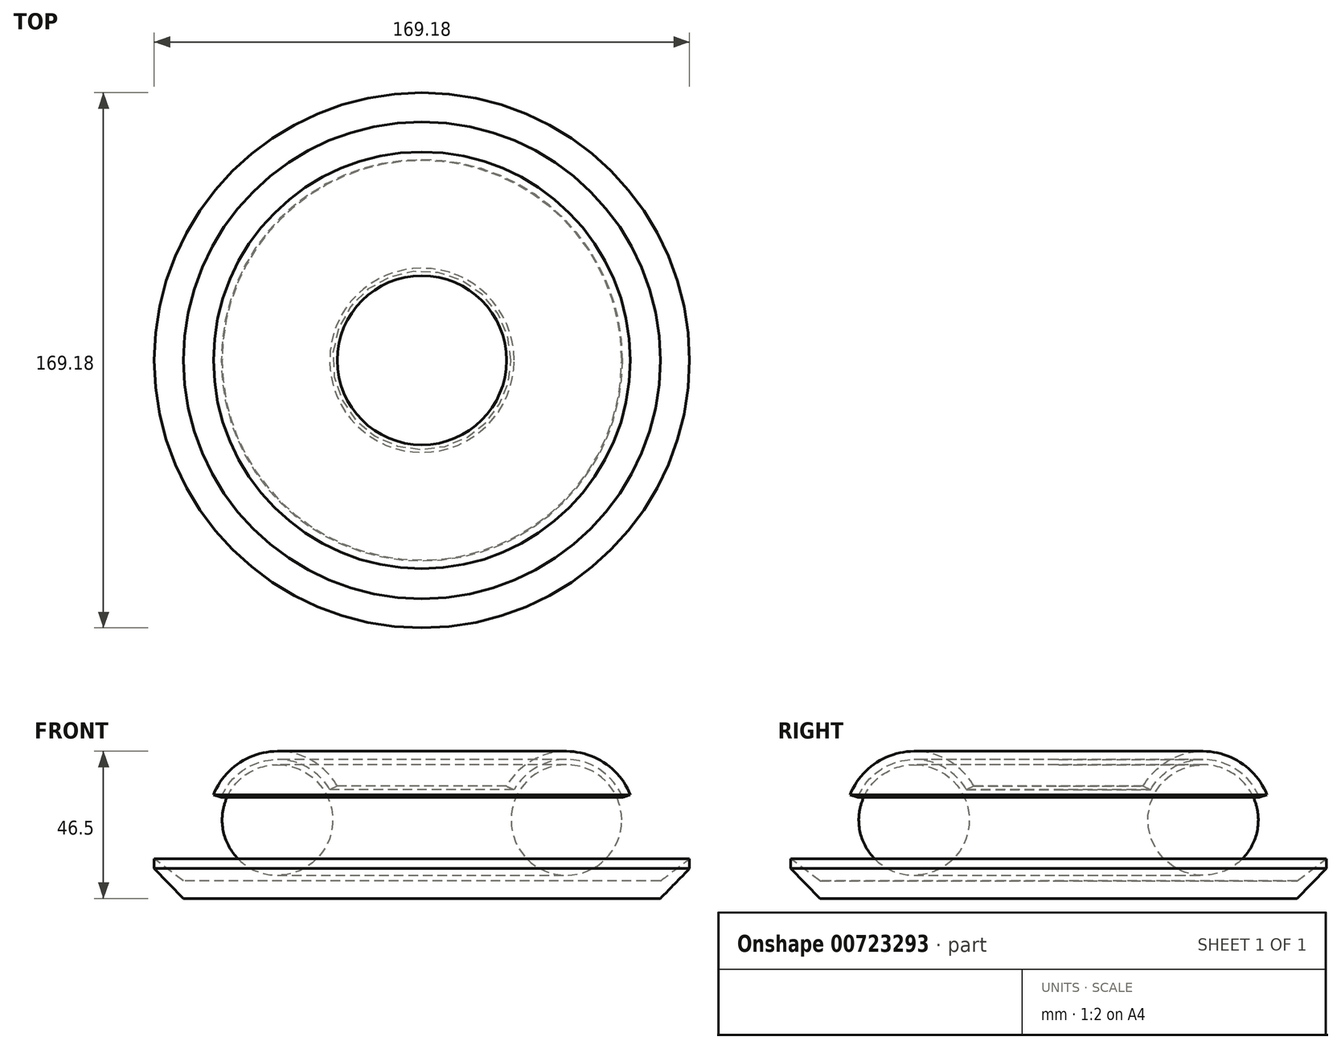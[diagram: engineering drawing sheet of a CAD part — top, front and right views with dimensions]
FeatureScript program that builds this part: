
annotation { "Feature Type Name" : "Feature", "Feature Type Description" : "" }
export const myFeature = defineFeature(function(context is Context, id is Id, definition is map)
    precondition{}
    {
        {
            var Q0;
            Q0=qCreatedBy(makeId("Right.planeOp"),FACE);
            var sketch = newSketch(context, id + "F0", { "sketchPlane" : qUnion([Q0])});
            skCircle(sketch, "E0", {"center": v(45.66, 0) * mm, "radius": 17.47 * mm});
            skLineSegment(sketch, "E1", {"start": v(0, 46.44) * mm, "end": v(0, -54.2) * mm, "construction": true});
            skArc(sketch, "E2", {"start": v(65.86, 7.98) * mm, "mid": v(47.15, 21.67) * mm, "end": v(26.74, 10.67) * mm});
            skArc(sketch, "E3", {"start": v(29.12, 9.6) * mm, "mid": v(47.03, 19.08) * mm, "end": v(63.4, 7.14) * mm});
            skLineSegment(sketch, "E4", {"start": v(26.74, 10.67) * mm, "end": v(29.12, 9.6) * mm});
            skLineSegment(sketch, "E5", {"start": v(65.86, 7.98) * mm, "end": v(63.4, 7.14) * mm});
            skLineSegment(sketch, "E6", {"start": v(0, -19.25) * mm, "end": v(75.37, -19.25) * mm});
            skLineSegment(sketch, "E7", {"start": v(75.37, -19.25) * mm, "end": v(84.59, -12.29) * mm});
            skLineSegment(sketch, "E8", {"start": v(84.59, -12.29) * mm, "end": v(84.59, -15.36) * mm});
            skLineSegment(sketch, "E9", {"start": v(84.59, -15.36) * mm, "end": v(75.37, -24.78) * mm});
            skLineSegment(sketch, "E10", {"start": v(75.37, -24.78) * mm, "end": v(0, -24.78) * mm});
            skLineSegment(sketch, "E11", {"start": v(0, -19.25) * mm, "end": v(0, -24.78) * mm});
            skSolve(sketch);
        }
        {
            var Q0;
            Q0=makeQuery(id+"F0.imprint","IMPRINT",FACE,{"disambiguationData":[TD([[makeQuery(id+"F0.imprint","IMPRINT",EDGE,{"derivedFrom":sQuery(id+"F0.wireOp",EDGE,"E2")}),1.0]])]});
            var Q1;
            Q1=makeQuery(id+"F0.imprint","IMPRINT",FACE,{"disambiguationData":[TD([[makeQuery(id+"F0.imprint","IMPRINT",EDGE,{"derivedFrom":sQuery(id+"F0.wireOp",EDGE,"E0")}),1.0]])]});
            var Q2;
            Q2=makeQuery(id+"F0.imprint","IMPRINT",FACE,{"disambiguationData":[TD([[makeQuery(id+"F0.imprint","IMPRINT",EDGE,{"derivedFrom":sQuery(id+"F0.wireOp",EDGE,"E6")}),-1.0]])]});
            var Q3;
            Q3=sQuery(id+"F0.wireOp",EDGE,"E1");
            revolve(context, id + "F1", {"surfaceOperationType" : NewSurfaceOperationType.NEW, "entities" : qUnion([Q0, Q1, Q2]), "axis" : qUnion([Q3]), "revolveType" : RevolveType.FULL});
        }
    });
